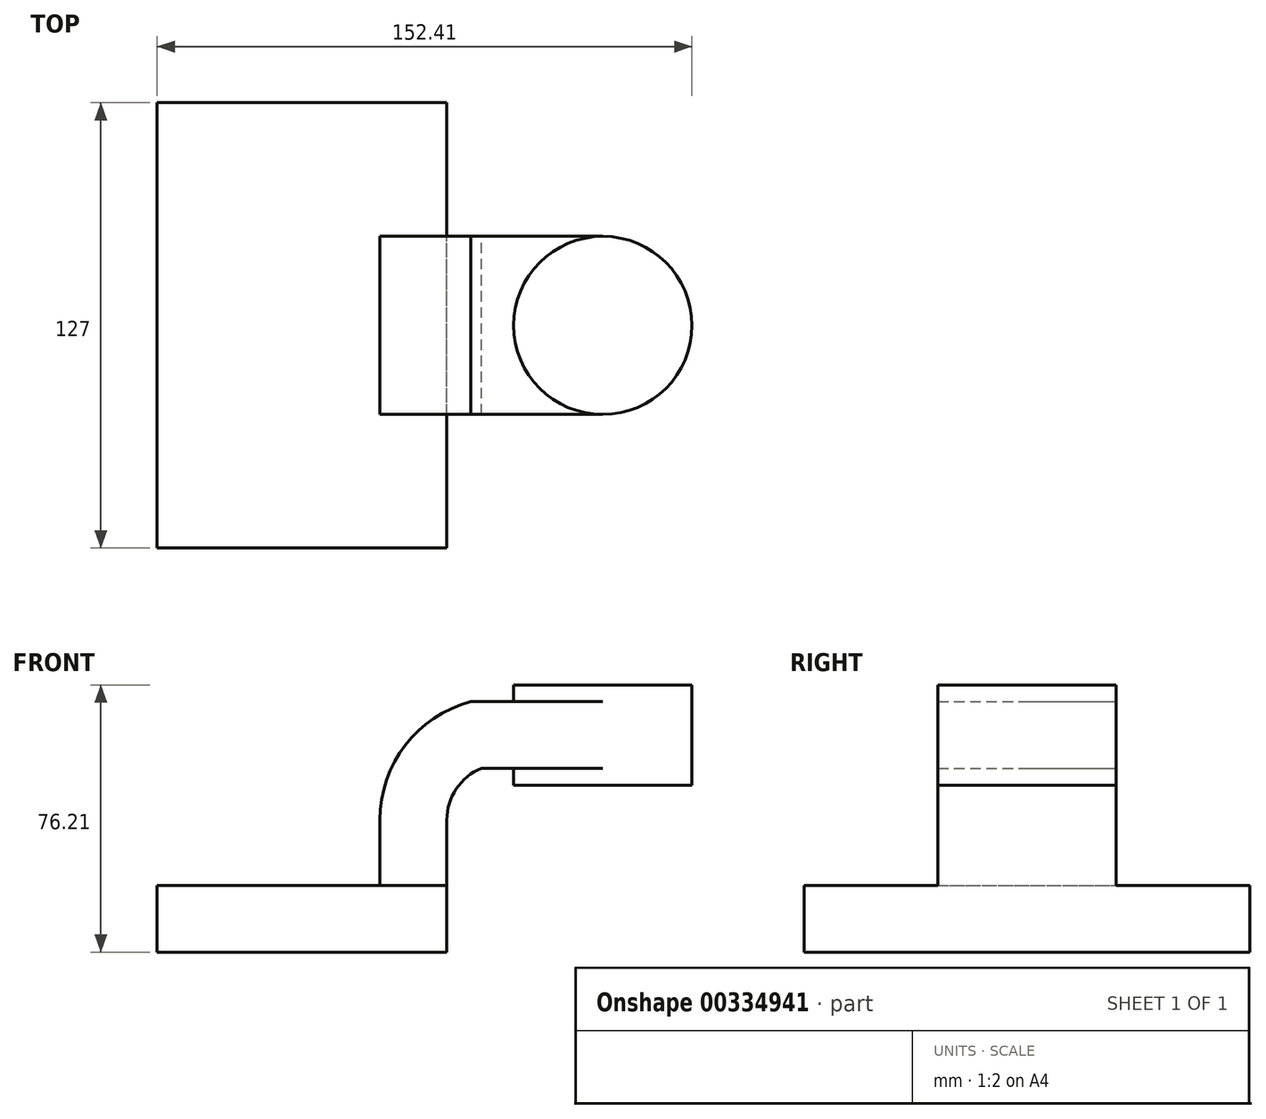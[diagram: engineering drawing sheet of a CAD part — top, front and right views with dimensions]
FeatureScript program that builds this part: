
annotation { "Feature Type Name" : "Feature", "Feature Type Description" : "" }
export const myFeature = defineFeature(function(context is Context, id is Id, definition is map)
    precondition{}
    {
        {
            var Q0;
            Q0=qCreatedBy(makeId("Front.planeOp"),FACE);
            var sketch = newSketch(context, id + "F0", { "sketchPlane" : qUnion([Q0])});
            skLineSegment(sketch, "E0.bottom", {"start": v(-41.28, 9.52) * mm, "end": v(41.27, 9.53) * mm});
            skLineSegment(sketch, "E0.top", {"start": v(-41.28, -9.53) * mm, "end": v(41.28, -9.53) * mm});
            skLineSegment(sketch, "E0.left", {"start": v(-41.28, 9.52) * mm, "end": v(-41.27, -9.53) * mm});
            skLineSegment(sketch, "E0.right", {"start": v(41.28, 9.53) * mm, "end": v(41.28, -9.52) * mm});
            skPoint(sketch, "E0.middle", {"position": v(0, 0) * mm});
            skLineSegment(sketch, "E1.bottom", {"start": v(60.32, 66.68) * mm, "end": v(111.12, 66.68) * mm});
            skLineSegment(sketch, "E1.top", {"start": v(60.32, 38.1) * mm, "end": v(111.12, 38.1) * mm});
            skLineSegment(sketch, "E1.left", {"start": v(60.32, 66.67) * mm, "end": v(60.32, 38.1) * mm});
            skLineSegment(sketch, "E1.right", {"start": v(111.12, 66.67) * mm, "end": v(111.12, 38.1) * mm});
            skPoint(sketch, "E1.middle", {"position": v(85.72, 52.39) * mm});
            skLineSegment(sketch, "E2", {"start": v(85.72, 42.88) * mm, "end": v(51.1, 42.88) * mm});
            skLineSegment(sketch, "E3", {"start": v(41.27, 9.53) * mm, "end": v(41.27, 28.2) * mm});
            skArc(sketch, "E4", {"start": v(41.27, 28.2) * mm, "mid": v(43.96, 37.03) * mm, "end": v(51.1, 42.88) * mm});
            skLineSegment(sketch, "E5.0", {"start": v(85.72, 61.93) * mm, "end": v(48.08, 61.93) * mm});
            skArc(sketch, "E5.1", {"start": v(22.23, 28.2) * mm, "mid": v(29.43, 49.45) * mm, "end": v(48.08, 61.93) * mm});
            skLineSegment(sketch, "E5.2", {"start": v(22.22, 9.53) * mm, "end": v(22.22, 28.2) * mm});
            skLineSegment(sketch, "E6", {"start": v(85.72, 38.1) * mm, "end": v(85.72, 66.68) * mm});
            skFitSpline(sketch, "E7", {"points": [v(-41.28, 9.52) * mm, v(48.08, 61.93) * mm], "startDerivative": vector(26.17, 86.47) * mm, "endDerivative": vector(144.23, 0.33) * mm});
            skSolve(sketch);
        }
        {
            var Q0;
            Q0=makeQuery(id+"F0.imprint","IMPRINT",FACE,{"disambiguationData":[TD([[makeQuery(id+"F0.imprint","IMPRINT",EDGE,{"derivedFrom":sQuery(id+"F0.wireOp",EDGE,"E0.top")}),1.0]])]});
            extrude(context, id + "F1", {"entities" : qUnion([Q0]), "endBound" : BoundingType.SYMMETRIC, "depth" : 127 * mm});
        }
        {
            var Q0;
            {var subQ4=sQuery(id+"F0.wireOp",EDGE,"E3");Q0=makeQuery(id+"F0.imprint","IMPRINT",FACE,{"disambiguationData":[TD([[makeQuery(id+"F0.imprint","IMPRINT",EDGE,{"derivedFrom":subQ4}),1.0]])]});}
            extrude(context, id + "F2", {"entities" : qUnion([Q0]), "operationType" : NewBodyOperationType.ADD, "endBound" : BoundingType.SYMMETRIC, "depth" : 50.8 * mm});
        }
        {
            var Q0;
            {var subQ0=sQuery(id+"F0.wireOp",EDGE,"E5.0");var subQ1=sQuery(id+"F0.wireOp",EDGE,"E1.left");var subQ2=makeQuery(id+"F0.imprint","INTERSECT",VERTEX,{"derivedFrom":[subQ1,subQ0]});Q0=makeQuery(id+"F0.imprint","IMPRINT",FACE,{"disambiguationData":[TD([[makeQuery(id+"F0.imprint","IMPRINT",EDGE,{"disambiguationData":[TD([[subQ2,-1.0]])],"derivedFrom":subQ1}),1.0]])]});}
            extrude(context, id + "F3", {"entities" : qUnion([Q0]), "operationType" : NewBodyOperationType.ADD, "endBound" : BoundingType.SYMMETRIC, "depth" : 50.8 * mm});
        }
        {
            var Q0;
            Q0=makeQuery(id+"F0.imprint","IMPRINT",FACE,{"disambiguationData":[TD([[makeQuery(id+"F0.imprint","IMPRINT",EDGE,{"derivedFrom":sQuery(id+"F0.wireOp",EDGE,"E5.1")}),1.0]])]});
            extrude(context, id + "F4", {"entities" : qUnion([Q0]), "operationType" : NewBodyOperationType.ADD, "endBound" : BoundingType.SYMMETRIC, "depth" : 15.88 * mm});
        }
        {
            var Q0;
            {var subQ0=sQuery(id+"F0.wireOp",EDGE,"E1.right");Q0=makeQuery(id+"F0.imprint","IMPRINT",FACE,{"disambiguationData":[TD([[makeQuery(id+"F0.imprint","IMPRINT",EDGE,{"derivedFrom":subQ0}),-1.0]])]});}
            var Q1;
            Q1=sQuery(id+"F0.wireOp",EDGE,"E6");
            revolve(context, id + "F5", {"operationType" : NewBodyOperationType.ADD, "entities" : qUnion([Q0]), "axis" : qUnion([Q1]), "revolveType" : RevolveType.FULL});
        }
    });
